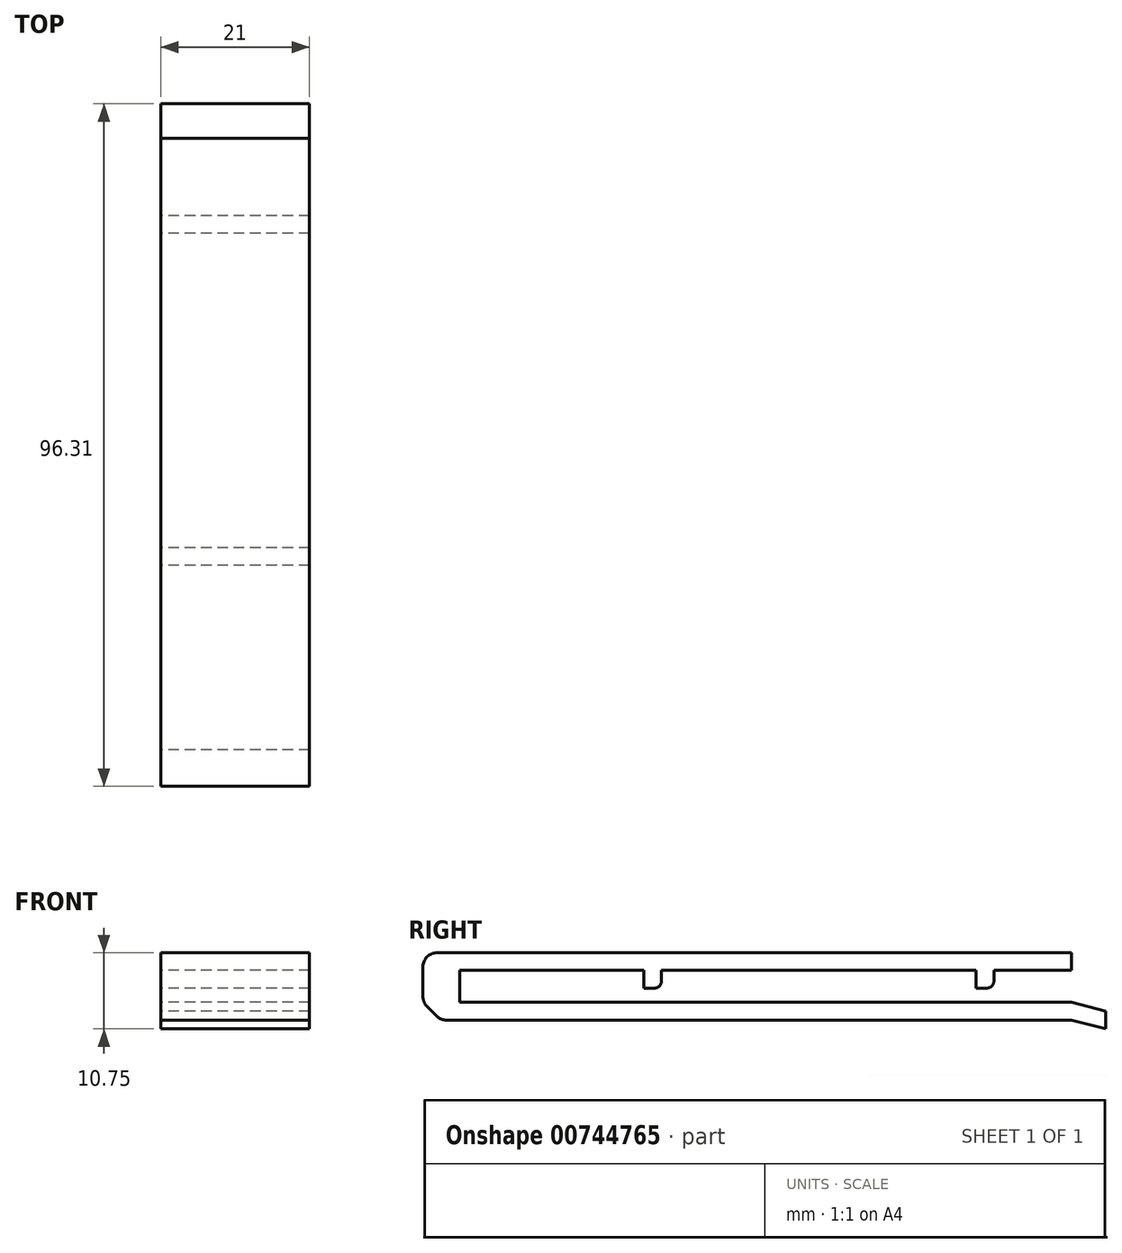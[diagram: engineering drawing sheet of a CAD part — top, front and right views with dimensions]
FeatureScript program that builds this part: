
annotation { "Feature Type Name" : "Feature", "Feature Type Description" : "" }
export const myFeature = defineFeature(function(context is Context, id is Id, definition is map)
    precondition{}
    {
        {
            var Q0;
            Q0=qCreatedBy(makeId("Right.planeOp"),FACE);
            var sketch = newSketch(context, id + "F0", { "sketchPlane" : qUnion([Q0])});
            skLineSegment(sketch, "E0.bottom", {"start": v(-8.01, 1.72) * mm, "end": v(80.99, 1.72) * mm});
            skLineSegment(sketch, "E0.top", {"start": v(-8.01, -0.78) * mm, "end": v(80.99, -0.78) * mm});
            skLineSegment(sketch, "E0.left", {"start": v(-8.01, 1.72) * mm, "end": v(-8.01, -0.78) * mm});
            skLineSegment(sketch, "E0.right", {"start": v(80.99, 1.72) * mm, "end": v(80.99, -0.78) * mm});
            skLineSegment(sketch, "E1", {"start": v(80.99, 1.72) * mm, "end": v(85.83, 0.47) * mm});
            skPoint(sketch, "E1.endSnap0", {"position": v(80.99, 0.47) * mm});
            skLineSegment(sketch, "E2", {"start": v(85.83, 0.47) * mm, "end": v(85.83, -2.03) * mm});
            skLineSegment(sketch, "E3", {"start": v(85.83, -2.03) * mm, "end": v(80.99, -0.78) * mm});
            skLineSegment(sketch, "E4", {"start": v(-8.01, -0.78) * mm, "end": v(-5.32, -0.78) * mm});
            skLineSegment(sketch, "E5", {"start": v(-5.32, -0.78) * mm, "end": v(-5.32, 8.72) * mm});
            skLineSegment(sketch, "E6", {"start": v(-5.32, 8.72) * mm, "end": v(-8.01, 8.72) * mm});
            skLineSegment(sketch, "E7", {"start": v(-8.01, 8.72) * mm, "end": v(-8.01, -0.78) * mm});
            skLineSegment(sketch, "E8", {"start": v(-8.01, 8.72) * mm, "end": v(-8.01, 6.22) * mm});
            skLineSegment(sketch, "E9", {"start": v(-8.01, 6.22) * mm, "end": v(-5.32, 6.22) * mm});
            skLineSegment(sketch, "E10", {"start": v(-5.32, 6.22) * mm, "end": v(-5.32, 8.72) * mm});
            skLineSegment(sketch, "E11", {"start": v(-8.01, 8.72) * mm, "end": v(80.99, 8.72) * mm});
            skLineSegment(sketch, "E12", {"start": v(80.99, 8.72) * mm, "end": v(80.99, 6.22) * mm});
            skLineSegment(sketch, "E13", {"start": v(80.99, 6.22) * mm, "end": v(-5.32, 6.22) * mm});
            skLineSegment(sketch, "E14", {"start": v(-8.01, -0.78) * mm, "end": v(-10.48, 1.72) * mm});
            skLineSegment(sketch, "E15", {"start": v(-10.48, 1.72) * mm, "end": v(-10.48, 7.24) * mm});
            skLineSegment(sketch, "E16", {"start": v(-10.48, 7.24) * mm, "end": v(-10.48, 8.72) * mm});
            skLineSegment(sketch, "E17", {"start": v(-10.48, 8.72) * mm, "end": v(-8.01, 8.72) * mm});
            skLineSegment(sketch, "E18", {"start": v(-5.32, 6.22) * mm, "end": v(20.68, 6.22) * mm});
            skLineSegment(sketch, "E19", {"start": v(20.68, 6.22) * mm, "end": v(20.68, 8.72) * mm});
            skLineSegment(sketch, "E20", {"start": v(20.68, 6.22) * mm, "end": v(20.68, 3.72) * mm});
            skLineSegment(sketch, "E21", {"start": v(20.68, 3.72) * mm, "end": v(23.18, 3.72) * mm});
            skLineSegment(sketch, "E22", {"start": v(23.18, 3.72) * mm, "end": v(23.18, 8.72) * mm});
            skLineSegment(sketch, "E23", {"start": v(23.18, 6.22) * mm, "end": v(67.57, 6.22) * mm});
            skLineSegment(sketch, "E24.bottom", {"start": v(67.57, 6.22) * mm, "end": v(70.07, 6.22) * mm});
            skLineSegment(sketch, "E24.top", {"start": v(67.57, 3.72) * mm, "end": v(70.07, 3.72) * mm});
            skLineSegment(sketch, "E24.left", {"start": v(67.57, 6.22) * mm, "end": v(67.57, 3.72) * mm});
            skLineSegment(sketch, "E24.right", {"start": v(70.07, 6.22) * mm, "end": v(70.07, 3.72) * mm});
            skSolve(sketch);
        }
        {
            var Q0;
            {var subQ1=sQuery(id+"F0.wireOp",EDGE,"E12");Q0=makeQuery(id+"F0.imprint","IMPRINT",FACE,{"disambiguationData":[TD([[makeQuery(id+"F0.imprint","IMPRINT",EDGE,{"derivedFrom":subQ1}),-1.0]])]});}
            var Q1;
            {var subQ5=sQuery(id+"F0.wireOp",EDGE,"E9");Q1=makeQuery(id+"F0.imprint","IMPRINT",FACE,{"disambiguationData":[TD([[makeQuery(id+"F0.imprint","IMPRINT",EDGE,{"derivedFrom":subQ5}),-1.0]])]});}
            var Q2;
            {var subQ3=sQuery(id+"F0.wireOp",EDGE,"E0.left");Q2=makeQuery(id+"F0.imprint","IMPRINT",FACE,{"disambiguationData":[TD([[makeQuery(id+"F0.imprint","IMPRINT",EDGE,{"derivedFrom":subQ3}),1.0]])]});}
            var Q3;
            {var subQ3=sQuery(id+"F0.wireOp",EDGE,"E0.right");Q3=makeQuery(id+"F0.imprint","IMPRINT",FACE,{"disambiguationData":[TD([[makeQuery(id+"F0.imprint","IMPRINT",EDGE,{"derivedFrom":subQ3}),-1.0]])]});}
            var Q4;
            {var subQ5=sQuery(id+"F0.wireOp",EDGE,"E19");Q4=makeQuery(id+"F0.imprint","IMPRINT",FACE,{"disambiguationData":[TD([[makeQuery(id+"F0.imprint","IMPRINT",EDGE,{"derivedFrom":subQ5}),1.0]])]});}
            var Q5;
            {var subQ3=sQuery(id+"F0.wireOp",EDGE,"E0.left");Q5=makeQuery(id+"F0.imprint","IMPRINT",FACE,{"disambiguationData":[TD([[makeQuery(id+"F0.imprint","IMPRINT",EDGE,{"derivedFrom":subQ3}),-1.0]])]});}
            var Q6;
            {var subQ0=sQuery(id+"F0.wireOp",EDGE,"E6");Q6=makeQuery(id+"F0.imprint","IMPRINT",FACE,{"disambiguationData":[TD([[makeQuery(id+"F0.imprint","IMPRINT",EDGE,{"derivedFrom":subQ0}),1.0]])]});}
            var Q7;
            {var subQ3=sQuery(id+"F0.wireOp",EDGE,"E19");Q7=makeQuery(id+"F0.imprint","IMPRINT",FACE,{"disambiguationData":[TD([[makeQuery(id+"F0.imprint","IMPRINT",EDGE,{"derivedFrom":subQ3}),-1.0]])]});}
            var Q8;
            Q8=makeQuery(id+"F0.imprint","IMPRINT",FACE,{"disambiguationData":[TD([[makeQuery(id+"F0.imprint","IMPRINT",EDGE,{"derivedFrom":sQuery(id+"F0.wireOp",EDGE,"E24.top")}),1.0]])]});
            var Q9;
            {var subQ0=sQuery(id+"F0.wireOp",EDGE,"E20");Q9=makeQuery(id+"F0.imprint","IMPRINT",FACE,{"disambiguationData":[TD([[makeQuery(id+"F0.imprint","IMPRINT",EDGE,{"derivedFrom":subQ0}),1.0]])]});}
            var Q10;
            Q10=makeQuery(id+"F0.imprint","IMPRINT",FACE,{"disambiguationData":[TD([[makeQuery(id+"F0.imprint","IMPRINT",EDGE,{"derivedFrom":sQuery(id+"F0.wireOp",EDGE,"E0.right")}),1.0]])]});
            extrude(context, id + "F1", {"entities" : qUnion([Q0, Q1, Q2, Q3, Q4, Q5, Q6, Q7, Q8, Q9, Q10]), "depth" : 21 * mm, "offsetDistance" : 25 * mm});
        }
        {
            var Q0;
            Q0=makeQuery(id+"F1.opExtrude","SWEPT_EDGE",EDGE,{"disambiguationData":[OSD([sQuery(id+"F0.wireOp",EDGE,"E16"),sQuery(id+"F0.wireOp",EDGE,"E17")])]});
            var Q1;
            Q1=makeQuery(id+"F1.opExtrude","SWEPT_EDGE",EDGE,{"disambiguationData":[OSD([sQuery(id+"F0.wireOp",EDGE,"E0.top"),sQuery(id+"F0.wireOp",EDGE,"E0.left"),sQuery(id+"F0.wireOp",EDGE,"E14")])]});
            var Q2;
            Q2=makeQuery(id+"F1.opExtrude","SWEPT_EDGE",EDGE,{"disambiguationData":[OSD([sQuery(id+"F0.wireOp",EDGE,"E14"),sQuery(id+"F0.wireOp",EDGE,"E15")])]});
            fillet(context, id + "F2", {"entities" : qUnion([Q0, Q1, Q2]), "radius" : 2 * mm, "tangentPropagation" : true, "allowEdgeOverflow" : false});
        }
        {
            var Q0;
            Q0=makeQuery(id+"F1.opExtrude","SWEPT_EDGE",EDGE,{"disambiguationData":[OSD([sQuery(id+"F0.wireOp",EDGE,"E21"),sQuery(id+"F0.wireOp",EDGE,"E22")])]});
            var Q1;
            Q1=makeQuery(id+"F1.opExtrude","SWEPT_EDGE",EDGE,{"disambiguationData":[OSD([sQuery(id+"F0.wireOp",EDGE,"E24.top"),sQuery(id+"F0.wireOp",EDGE,"E24.right")])]});
            fillet(context, id + "F3", {"entities" : qUnion([Q0, Q1]), "radius" : 1 * mm, "tangentPropagation" : true, "allowEdgeOverflow" : false});
        }
    });
